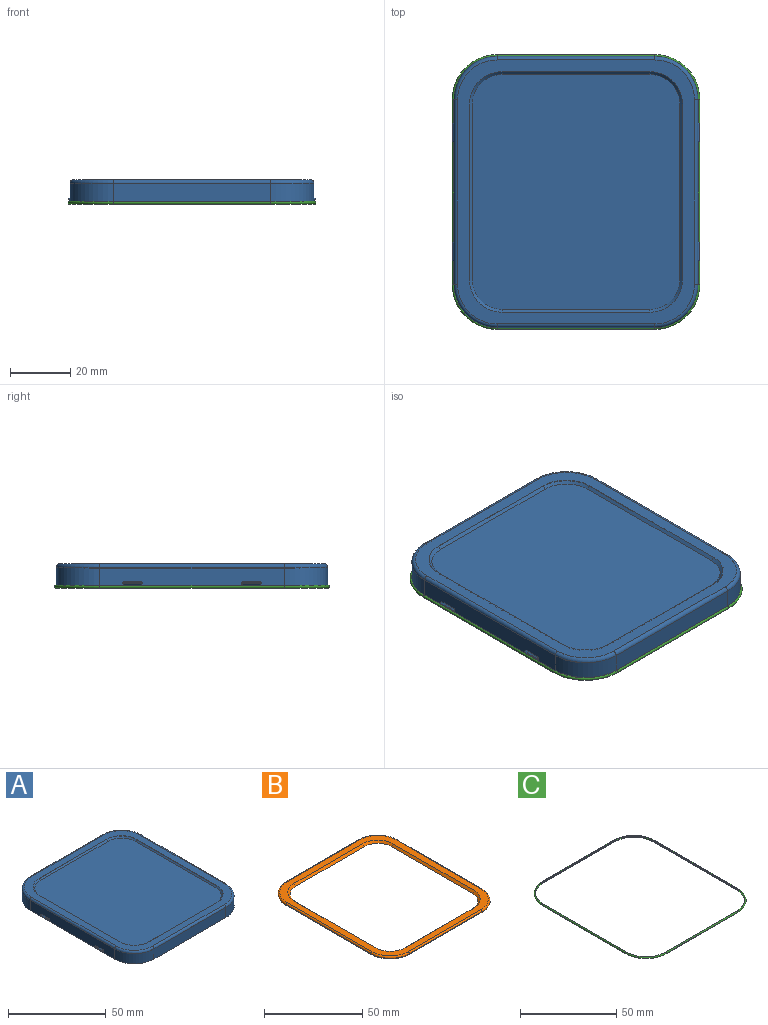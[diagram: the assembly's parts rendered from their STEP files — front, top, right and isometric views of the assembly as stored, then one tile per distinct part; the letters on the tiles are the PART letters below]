
ASSEMBLY  parts=3 mates=1
PART A: 113 faces, bbox 83.1x92.1x7.6 mm
  f0: plane 89.79x80.72mm, normal (0,0,-1), area 100.2mm2, adj f8,f9,f10,f11,f12,f13,f14,f15
  f1: plane 5.49x0.49mm, normal (-0.71,0,-0.71), area 3.8mm2, adj f5,f14,f100,f107
  f2: plane 5.49x0.49mm, normal (-0.71,0,0.71), area 3.8mm2, adj f5,f14,f98,f109
  f3: plane 5.49x0.49mm, normal (0.71,0,-0.71), area 3.8mm2, adj f6,f10,f92,f101
  f4: plane 5.49x0.49mm, normal (0.71,0,0.71), area 3.8mm2, adj f6,f10,f94,f103
  f5: cylinder r=0.2mm len=5.49mm, axis (0,1,0), area 1.8mm2, adj f1,f2,f99,f108
  f6: cylinder r=0.2mm len=5.49mm, axis (0,1,0), area 1.8mm2, adj f3,f4,f93,f102
  f7: plane 87.41x78.34mm, normal (0,0,1), area 1181.6mm2, adj f16,f17,f18,f19,f20,f21,f22,f23
  f8: plane 52.15x6.43mm, normal (0,-1,0), area 335.3mm2, adj f0,f9,f15,f20
  f9: cylinder r=14.29mm len=14.29mm, axis (0,0,-1), area 144.3mm2, adj f0,f8,f10,f18
  f10: plane 61.21x6.43mm, normal (1,0,0), area 377.9mm2, adj f0,f3,f4,f9,f11,f16,f38,f40
  f11: cylinder r=14.29mm len=14.29mm, axis (0,0,-1), area 144.3mm2, adj f0,f10,f12,f17
  f12: plane 52.15x6.43mm, normal (0,1,0), area 335.3mm2, adj f0,f11,f13,f19
  f13: cylinder r=14.29mm len=14.29mm, axis (0,0,-1), area 144.3mm2, adj f0,f12,f14,f21
  f14: plane 61.21x6.43mm, normal (-1,0,0), area 377.9mm2, adj f0,f1,f2,f13,f15,f23,f34,f35
  f15: cylinder r=14.29mm len=14.29mm, axis (0,0,-1), area 144.3mm2, adj f0,f8,f14,f22
  f16: cylinder r=1.19mm len=61.21mm, axis (0,-1,0), area 114.5mm2, adj f7,f10,f17,f18
  f17: torus R=13.1mm, axis (0,0,1), area 40.7mm2, adj f7,f11,f16,f19
  f18: torus R=13.1mm, axis (0,0,1), area 40.7mm2, adj f7,f9,f16,f20
  f19: cylinder r=1.19mm len=52.15mm, axis (1,0,0), area 97.5mm2, adj f7,f12,f17,f21
  f20: cylinder r=1.19mm len=52.15mm, axis (-1,0,0), area 97.5mm2, adj f7,f8,f18,f22
  f21: torus R=13.1mm, axis (0,0,1), area 40.7mm2, adj f7,f13,f19,f23
  f22: torus R=13.1mm, axis (0,0,1), area 40.7mm2, adj f7,f15,f20,f23
  f23: cylinder r=1.19mm len=61.21mm, axis (0,1,0), area 114.5mm2, adj f7,f14,f21,f22
  f24: plane 77.85x68.78mm, normal (0,0,1), area 5270.6mm2, adj f25,f26,f27,f28,f29,f30,f31,f32
  f25: cone r=9.53mm half-angle=45deg, axis (0,0,1), area 20.4mm2, adj f7,f24,f26,f27
  f26: plane 58.04x0.89mm, normal (0.71,0,0.71), area 73mm2, adj f7,f24,f25,f28
  f27: plane 48.97x0.89mm, normal (0,-0.71,0.71), area 61.6mm2, adj f7,f24,f25,f29
  f28: cone r=9.53mm half-angle=45deg, axis (0,0,1), area 20.4mm2, adj f7,f24,f26,f30
  f29: cone r=9.53mm half-angle=45deg, axis (0,0,1), area 20.4mm2, adj f7,f24,f27,f31
  f30: plane 48.97x0.89mm, normal (0,0.71,0.71), area 61.6mm2, adj f7,f24,f28,f32
  f31: plane 58.04x0.89mm, normal (-0.71,0,0.71), area 73mm2, adj f7,f24,f29,f32
  f32: cone r=9.53mm half-angle=45deg, axis (0,0,1), area 20.4mm2, adj f7,f24,f30,f31
  f33: cylinder r=0.2mm len=5.49mm, axis (0,1,0), area 1.8mm2, adj f34,f35,f96,f111
  f34: plane 5.49x0.49mm, normal (-0.71,0,-0.71), area 3.8mm2, adj f14,f33,f97,f112
  f35: plane 5.49x0.49mm, normal (-0.71,0,0.71), area 3.8mm2, adj f14,f33,f95,f110
  f36: plane 0.05x0.02mm, normal (0,-1,0), area 0mm2, adj f14,f110,f112
  f37: plane 0.05x0.02mm, normal (0,1,0), area 0mm2, adj f14,f107,f109
  f38: plane 5.49x0.49mm, normal (0.71,0,-0.71), area 3.8mm2, adj f10,f39,f89,f104
  f39: cylinder r=0.2mm len=5.49mm, axis (0,1,0), area 1.8mm2, adj f38,f40,f90,f105
  f40: plane 5.49x0.49mm, normal (0.71,0,0.71), area 3.8mm2, adj f10,f39,f91,f106
  f41: plane 0.05x0.02mm, normal (0,-1,0), area 0mm2, adj f10,f104,f106
  f42: plane 0.05x0.02mm, normal (0,1,0), area 0mm2, adj f10,f101,f103
  f43: plane 0.05x0.02mm, normal (0,-1,0), area 0mm2, adj f10,f92,f94
  f44: plane 0.05x0.02mm, normal (0,1,0), area 0mm2, adj f10,f89,f91
  f45: plane 0.05x0.02mm, normal (0,-1,0), area 0mm2, adj f14,f98,f100
  f46: plane 0.05x0.02mm, normal (0,1,0), area 0mm2, adj f14,f95,f97
  f47: plane 5.72x0.5mm, normal (0.71,0,0.71), area 4.1mm2, adj f48,f58,f80,f87
  f48: plane 5.72x0.5mm, normal (0.71,0,-0.71), area 4.1mm2, adj f47,f58,f80,f87
  f49: plane 5.72x0.5mm, normal (-0.71,0,0.71), area 4.1mm2, adj f50,f54,f84,f85
  f50: plane 5.72x0.5mm, normal (-0.71,0,-0.71), area 4.1mm2, adj f49,f54,f84,f85
  f51: plane 87.41x78.34mm, normal (0,0,-1), area 1144.5mm2, adj f60,f61,f62,f63,f64,f65,f66,f67
  f52: plane 52.15x6.43mm, normal (0,1,0), area 335.3mm2, adj f0,f53,f59,f64
  f53: cylinder r=13.97mm len=13.97mm, axis (0,0,-1), area 141.1mm2, adj f0,f52,f54,f62
  f54: plane 61.21x6.43mm, normal (-1,0,0), area 382.1mm2, adj f0,f49,f50,f53,f55,f60,f81,f82
  f55: cylinder r=13.97mm len=13.97mm, axis (0,0,-1), area 141.1mm2, adj f0,f54,f56,f61
  f56: plane 52.15x6.43mm, normal (0,-1,0), area 335.3mm2, adj f0,f55,f57,f63
  f57: cylinder r=13.97mm len=13.97mm, axis (0,0,-1), area 141.1mm2, adj f0,f56,f58,f65
  f58: plane 61.21x6.43mm, normal (1,0,0), area 382.1mm2, adj f0,f47,f48,f57,f59,f67,f77,f78
  f59: cylinder r=13.97mm len=13.97mm, axis (0,0,-1), area 141.1mm2, adj f0,f52,f58,f66
  f60: cylinder r=0.87mm len=61.21mm, axis (0,-1,0), area 84mm2, adj f51,f54,f61,f62
  f61: torus R=13.1mm, axis (0,0,1), area 29.4mm2, adj f51,f55,f60,f63
  f62: torus R=13.1mm, axis (0,0,1), area 29.4mm2, adj f51,f53,f60,f64
  f63: cylinder r=0.87mm len=52.15mm, axis (1,0,0), area 71.5mm2, adj f51,f56,f61,f65
  f64: cylinder r=0.87mm len=52.15mm, axis (-1,0,0), area 71.5mm2, adj f51,f52,f62,f66
  f65: torus R=13.1mm, axis (0,0,1), area 29.4mm2, adj f51,f57,f63,f67
  f66: torus R=13.1mm, axis (0,0,1), area 29.4mm2, adj f51,f59,f64,f67
  f67: cylinder r=0.87mm len=61.21mm, axis (0,1,0), area 84mm2, adj f51,f58,f65,f66
  f68: plane 78.11x69.05mm, normal (0,0,-1), area 5307mm2, adj f69,f70,f71,f72,f73,f74,f75,f76
  f69: cone r=9.75mm half-angle=45deg, axis (0,0,1), area 20.7mm2, adj f51,f68,f70,f71
  f70: plane 58.04x0.89mm, normal (-0.71,0,-0.71), area 73mm2, adj f51,f68,f69,f72
  f71: plane 48.97x0.89mm, normal (0,0.71,-0.71), area 61.6mm2, adj f51,f68,f69,f73
  f72: cone r=9.75mm half-angle=45deg, axis (0,0,1), area 20.7mm2, adj f51,f68,f70,f74
  f73: cone r=9.75mm half-angle=45deg, axis (0,0,1), area 20.7mm2, adj f51,f68,f71,f75
  f74: plane 48.97x0.89mm, normal (0,-0.71,-0.71), area 61.6mm2, adj f51,f68,f72,f76
  f75: plane 58.04x0.89mm, normal (0.71,0,-0.71), area 73mm2, adj f51,f68,f73,f76
  f76: cone r=9.75mm half-angle=45deg, axis (0,0,1), area 20.7mm2, adj f51,f68,f74,f75
  f77: plane 5.72x0.5mm, normal (0.71,0,0.71), area 4.1mm2, adj f58,f78,f79,f88
  f78: plane 5.72x0.5mm, normal (0.71,0,-0.71), area 4.1mm2, adj f58,f77,f79,f88
  f79: plane 1.01x0.5mm, normal (0,1,0), area 0.3mm2, adj f58,f77,f78
  f80: plane 1.01x0.5mm, normal (0,-1,0), area 0.3mm2, adj f47,f48,f58
  f81: plane 5.72x0.5mm, normal (-0.71,0,0.71), area 4.1mm2, adj f54,f82,f83,f86
  f82: plane 5.72x0.5mm, normal (-0.71,0,-0.71), area 4.1mm2, adj f54,f81,f83,f86
  f83: plane 1.01x0.5mm, normal (0,1,0), area 0.3mm2, adj f54,f81,f82
  f84: plane 1.01x0.5mm, normal (0,-1,0), area 0.3mm2, adj f49,f50,f54
  f85: plane 1.01x0.5mm, normal (0,1,0), area 0.3mm2, adj f49,f50,f54
  f86: plane 1.01x0.5mm, normal (0,-1,0), area 0.3mm2, adj f54,f81,f82
  f87: plane 1.01x0.5mm, normal (0,1,0), area 0.3mm2, adj f47,f48,f58
  f88: plane 1.01x0.5mm, normal (0,-1,0), area 0.3mm2, adj f58,f77,f78
  f89: cylinder r=0.43mm len=0.8mm, axis (0.71,0,0.71), area 0.3mm2, adj f10,f38,f44,f90
  f90: bspline ~0.61x0.51mm, area 0.1mm2, adj f39,f89,f91
  f91: cylinder r=0.43mm len=0.8mm, axis (-0.71,0,0.71), area 0.3mm2, adj f10,f40,f44,f90
  f92: cylinder r=0.43mm len=0.8mm, axis (-0.71,0,-0.71), area 0.3mm2, adj f3,f10,f43,f93
  f93: bspline ~0.61x0.51mm, area 0.1mm2, adj f6,f92,f94
  f94: cylinder r=0.43mm len=0.8mm, axis (0.71,0,-0.71), area 0.3mm2, adj f4,f10,f43,f93
  f95: cylinder r=0.43mm len=0.8mm, axis (-0.71,0,-0.71), area 0.3mm2, adj f14,f35,f46,f96
  f96: bspline ~0.61x0.51mm, area 0.1mm2, adj f33,f95,f97
  f97: cylinder r=0.43mm len=0.8mm, axis (0.71,0,-0.71), area 0.3mm2, adj f14,f34,f46,f96
  f98: cylinder r=0.43mm len=0.8mm, axis (0.71,0,0.71), area 0.3mm2, adj f2,f14,f45,f99
  f99: bspline ~0.61x0.51mm, area 0.1mm2, adj f5,f98,f100
  f100: cylinder r=0.43mm len=0.8mm, axis (-0.71,0,0.71), area 0.3mm2, adj f1,f14,f45,f99
  f101: cylinder r=0.43mm len=0.8mm, axis (0.71,0,0.71), area 0.3mm2, adj f3,f10,f42,f102
  f102: bspline ~0.61x0.51mm, area 0.1mm2, adj f6,f101,f103
  f103: cylinder r=0.43mm len=0.8mm, axis (-0.71,0,0.71), area 0.3mm2, adj f4,f10,f42,f102
  f104: cylinder r=0.43mm len=0.8mm, axis (-0.71,0,-0.71), area 0.3mm2, adj f10,f38,f41,f105
  f105: bspline ~0.61x0.51mm, area 0.1mm2, adj f39,f104,f106
  f106: cylinder r=0.43mm len=0.8mm, axis (0.71,0,-0.71), area 0.3mm2, adj f10,f40,f41,f105
  f107: cylinder r=0.43mm len=0.8mm, axis (0.71,0,-0.71), area 0.3mm2, adj f1,f14,f37,f108
  f108: bspline ~0.61x0.51mm, area 0.1mm2, adj f5,f107,f109
  f109: cylinder r=0.43mm len=0.8mm, axis (-0.71,0,-0.71), area 0.3mm2, adj f2,f14,f37,f108
  f110: cylinder r=0.43mm len=0.8mm, axis (0.71,0,0.71), area 0.3mm2, adj f14,f35,f36,f111
  f111: bspline ~0.61x0.51mm, area 0.1mm2, adj f33,f110,f112
  f112: cylinder r=0.43mm len=0.8mm, axis (-0.71,0,0.71), area 0.3mm2, adj f14,f34,f36,f111
PART B: 26 faces, bbox 82.4x91.2x1.2 mm
  f0: plane 87.15x78.33mm, normal (0,0,1), area 1082.7mm2, adj f10,f11,f12,f13,f14,f15,f16,f17
  f1: plane 88.9x80.09mm, normal (0,0,-1), area 1693.4mm2, adj f2,f3,f4,f5,f6,f7,f8,f9
  f2: plane 52.12x0.33mm, normal (0,-1,0), area 17.2mm2, adj f1,f3,f9,f14
  f3: cylinder r=13.98mm len=13.98mm, axis (0,0,-1), area 7.3mm2, adj f1,f2,f4,f16
  f4: plane 60.93x0.33mm, normal (1,0,0), area 20.1mm2, adj f1,f3,f5,f17
  f5: cylinder r=13.98mm len=13.98mm, axis (0,0,-1), area 7.3mm2, adj f1,f4,f6,f15
  f6: plane 52.12x0.33mm, normal (0,1,0), area 17.2mm2, adj f1,f5,f7,f13
  f7: cylinder r=13.98mm len=13.98mm, axis (0,0,-1), area 7.3mm2, adj f1,f6,f8,f11
  f8: plane 60.93x0.33mm, normal (-1,0,0), area 20.1mm2, adj f1,f7,f9,f10
  f9: cylinder r=13.98mm len=13.98mm, axis (0,0,-1), area 7.3mm2, adj f1,f2,f8,f12
  f10: cylinder r=0.88mm len=60.93mm, axis (0,1,0), area 83.9mm2, adj f0,f8,f11,f12
  f11: torus R=13.11mm, axis (0,0,1), area 29.5mm2, adj f0,f7,f10,f13
  f12: torus R=13.11mm, axis (0,0,1), area 29.5mm2, adj f0,f9,f10,f14
  f13: cylinder r=0.88mm len=52.12mm, axis (1,0,0), area 71.7mm2, adj f0,f6,f11,f15
  f14: cylinder r=0.88mm len=52.12mm, axis (-1,0,0), area 71.7mm2, adj f0,f2,f12,f16
  f15: torus R=13.11mm, axis (0,0,1), area 29.5mm2, adj f0,f5,f13,f17
  f16: torus R=13.11mm, axis (0,0,1), area 29.5mm2, adj f0,f3,f14,f17
  f17: cylinder r=0.88mm len=60.93mm, axis (0,-1,0), area 83.9mm2, adj f0,f4,f15,f16
  f18: plane 58.42x1.21mm, normal (0.71,0,0.71), area 99.7mm2, adj f0,f1,f19,f20
  f19: cone r=9.53mm half-angle=45deg, axis (0,0,1), area 27.3mm2, adj f0,f1,f18,f21
  f20: cone r=9.53mm half-angle=45deg, axis (0,0,1), area 27.3mm2, adj f0,f1,f18,f22
  f21: plane 49.61x1.21mm, normal (0,-0.71,0.71), area 84.6mm2, adj f0,f1,f19,f23
  f22: plane 49.61x1.21mm, normal (0,0.71,0.71), area 84.6mm2, adj f0,f1,f20,f24
  f23: cone r=9.53mm half-angle=45deg, axis (0,0,1), area 27.3mm2, adj f0,f1,f21,f25
  f24: cone r=9.53mm half-angle=45deg, axis (0,0,1), area 27.3mm2, adj f0,f1,f22,f25
  f25: plane 58.42x1.21mm, normal (-0.71,0,0.71), area 99.7mm2, adj f0,f1,f23,f24
PART C: 25 faces, bbox 84.5x93.4x1 mm
  f0: cone r=14.31mm half-angle=16.8deg, axis (0,0,-1), area 7.2mm2, adj f1,f2,f20,f24
  f1: torus R=14.45mm, axis (0,0,-1), area 55.2mm2, adj f0,f3,f21,f22
  f2: plane 52.15x0.3mm, normal (0,0.96,-0.29), area 16.6mm2, adj f0,f3,f4,f5
  f3: cylinder r=0.48mm len=52.15mm, axis (-1,0,0), area 126mm2, adj f1,f2,f6,f22
  f4: cylinder r=0.17mm len=52.15mm, axis (-1,0,0), area 43.1mm2, adj f2,f7,f22,f24
  f5: cone r=14.31mm half-angle=16.8deg, axis (0,0,-1), area 7.2mm2, adj f2,f6,f7,f8
  f6: torus R=14.45mm, axis (0,0,-1), area 55.2mm2, adj f3,f5,f9,f22
  f7: torus R=14.45mm, axis (0,0,-1), area 18.8mm2, adj f4,f5,f10,f22
  f8: plane 61.11x0.3mm, normal (-0.96,0,-0.29), area 19.4mm2, adj f5,f9,f10,f11
  f9: cylinder r=0.48mm len=61.11mm, axis (0,-1,0), area 147.6mm2, adj f6,f8,f12,f22
  f10: cylinder r=0.17mm len=61.11mm, axis (0,-1,0), area 50.5mm2, adj f7,f8,f13,f22
  f11: cone r=14.31mm half-angle=16.8deg, axis (0,0,-1), area 7.2mm2, adj f8,f12,f13,f14
  f12: torus R=14.45mm, axis (0,0,-1), area 55.2mm2, adj f9,f11,f15,f22
  f13: torus R=14.45mm, axis (0,0,-1), area 18.8mm2, adj f10,f11,f16,f22
  f14: plane 52.15x0.3mm, normal (0,-0.96,-0.29), area 16.6mm2, adj f11,f15,f16,f17
  f15: cylinder r=0.48mm len=52.15mm, axis (1,0,0), area 126mm2, adj f12,f14,f18,f22
  f16: cylinder r=0.17mm len=52.15mm, axis (1,0,0), area 43.1mm2, adj f13,f14,f19,f22
  f17: cone r=14.31mm half-angle=16.8deg, axis (0,0,-1), area 7.2mm2, adj f14,f18,f19,f20
  f18: torus R=14.45mm, axis (0,0,-1), area 55.2mm2, adj f15,f17,f21,f22
  f19: torus R=14.45mm, axis (0,0,-1), area 18.8mm2, adj f16,f17,f22,f23
  f20: plane 61.11x0.3mm, normal (0.96,0,-0.29), area 19.4mm2, adj f0,f17,f21,f23
  f21: cylinder r=0.48mm len=61.11mm, axis (0,1,0), area 147.6mm2, adj f1,f18,f20,f22
  f22: plane 89.69x80.72mm, normal (0,0,1), area 100.1mm2, adj f1,f3,f4,f6,f7,f9,f10,f12
  f23: cylinder r=0.17mm len=61.11mm, axis (0,1,0), area 50.5mm2, adj f19,f20,f22,f24
  f24: torus R=14.45mm, axis (0,0,-1), area 18.8mm2, adj f0,f4,f22,f23
PLACE A t=(0,-0.05,-3.25)mm fixed
PLACE B t=(0,-0.05,2.85)mm
PLACE C t=(0,-0.05,-3.25)mm fixed
MATE fastened B.f0 <-> A.f51  axis (0,0,1) through (-39.17,-0.05,4.06)mm
